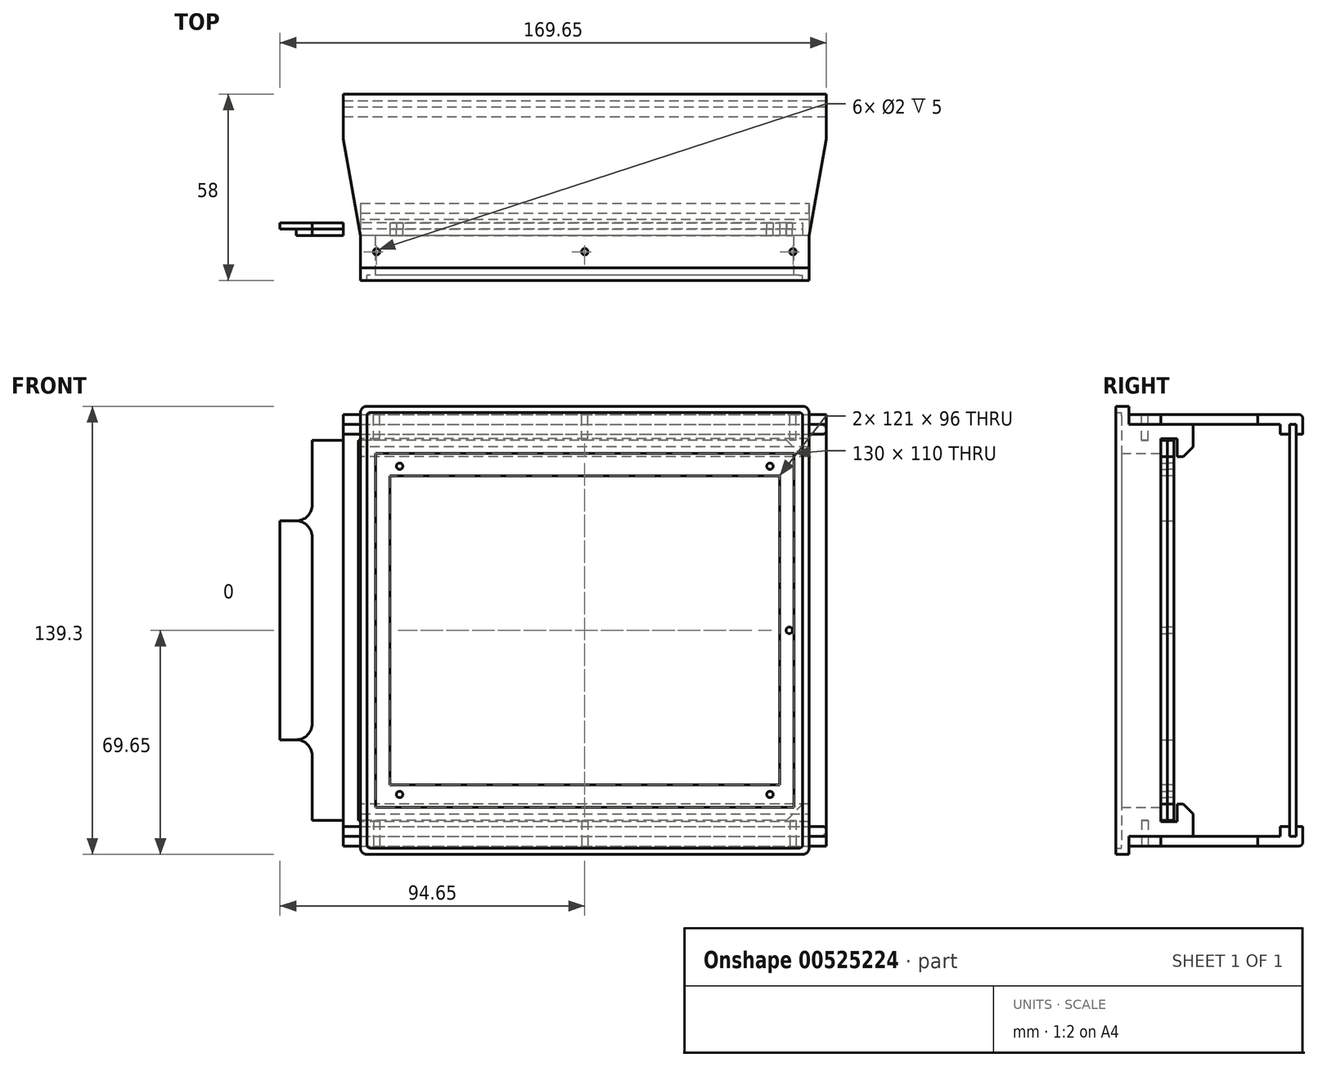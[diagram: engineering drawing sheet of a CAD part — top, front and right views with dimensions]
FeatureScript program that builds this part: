
annotation { "Feature Type Name" : "Feature", "Feature Type Description" : "" }
export const myFeature = defineFeature(function(context is Context, id is Id, definition is map)
    precondition{}
    {
        {
            var Q0;
            Q0=qCreatedBy(makeId("Front.planeOp"),FACE);
            var sketch = newSketch(context, id + "F0", { "sketchPlane" : qUnion([Q0])});
            skLineSegment(sketch, "E0.bottom", {"start": v(69.65, 69.65) * mm, "end": v(-69.65, 69.65) * mm});
            skLineSegment(sketch, "E0.top", {"start": v(69.65, -69.65) * mm, "end": v(-69.65, -69.65) * mm});
            skLineSegment(sketch, "E0.left", {"start": v(69.65, 69.65) * mm, "end": v(69.65, -69.65) * mm});
            skLineSegment(sketch, "E0.right", {"start": v(-69.65, 69.65) * mm, "end": v(-69.65, -69.65) * mm});
            skPoint(sketch, "E0.middle", {"position": v(0, 0) * mm});
            skLineSegment(sketch, "E1.bottom", {"start": v(65, 55) * mm, "end": v(-65, 55) * mm});
            skLineSegment(sketch, "E1.top", {"start": v(65, -55) * mm, "end": v(-65, -55) * mm});
            skLineSegment(sketch, "E1.left", {"start": v(65, 55) * mm, "end": v(65, -55) * mm});
            skLineSegment(sketch, "E1.right", {"start": v(-65, 55) * mm, "end": v(-65, -55) * mm});
            skSolve(sketch);
        }
        {
            var Q0;
            Q0=makeQuery(id+"F0.imprint","IMPRINT",FACE,{"disambiguationData":[TD([[makeQuery(id+"F0.imprint","IMPRINT",EDGE,{"derivedFrom":sQuery(id+"F0.wireOp",EDGE,"E0.bottom")}),1.0]])]});
            extrude(context, id + "F1", {"entities" : qUnion([Q0]), "depth" : 2.3 * mm, "offsetDistance" : 25 * mm});
        }
        {
            var Q0;
            Q0=makeQuery(id+"F1.opExtrude","CAP_FACE",FACE,{"disambiguationData":[OSD([sQuery(id+"F0.wireOp",EDGE,"E0.bottom"),sQuery(id+"F0.wireOp",EDGE,"E0.top"),sQuery(id+"F0.wireOp",EDGE,"E0.left"),sQuery(id+"F0.wireOp",EDGE,"E0.right"),sQuery(id+"F0.wireOp",EDGE,"E1.bottom"),sQuery(id+"F0.wireOp",EDGE,"E1.top"),sQuery(id+"F0.wireOp",EDGE,"E1.left"),sQuery(id+"F0.wireOp",EDGE,"E1.right")])],"isStart":true});
            var sketch = newSketch(context, id + "F2", { "sketchPlane" : qUnion([Q0])});
            skLineSegment(sketch, "E2.0", {"start": v(-65, 55) * mm, "end": v(65, 55) * mm});
            skLineSegment(sketch, "E3.0", {"start": v(-65, 55) * mm, "end": v(-65, -55) * mm});
            skLineSegment(sketch, "E3.1", {"start": v(-65, -55) * mm, "end": v(65, -55) * mm});
            skLineSegment(sketch, "E3.2", {"start": v(65, 55) * mm, "end": v(65, -55) * mm});
            skLineSegment(sketch, "E4.bottom", {"start": v(69.65, 64) * mm, "end": v(-69.65, 64) * mm});
            skLineSegment(sketch, "E4.top", {"start": v(69.65, -64) * mm, "end": v(-69.65, -64) * mm});
            skLineSegment(sketch, "E4.left", {"start": v(69.65, 64) * mm, "end": v(69.65, -64) * mm});
            skLineSegment(sketch, "E4.right", {"start": v(-69.65, 64) * mm, "end": v(-69.65, -64) * mm});
            skPoint(sketch, "E4.middle", {"position": v(0, 0) * mm});
            skSolve(sketch);
        }
        {
            var Q0;
            Q0 = qSketchRegion(id + "F2", true);
            extrude(context, id + "F3", {"entities" : qUnion([Q0]), "operationType" : NewBodyOperationType.ADD, "depth" : 10 * mm, "offsetDistance" : 25 * mm});
        }
        {
            var Q0;
            Q0=makeQuery(id+"F1.opExtrude","CAP_FACE",FACE,{"disambiguationData":[OSD([sQuery(id+"F0.wireOp",EDGE,"E0.bottom"),sQuery(id+"F0.wireOp",EDGE,"E0.top"),sQuery(id+"F0.wireOp",EDGE,"E0.left"),sQuery(id+"F0.wireOp",EDGE,"E0.right"),sQuery(id+"F0.wireOp",EDGE,"E1.bottom"),sQuery(id+"F0.wireOp",EDGE,"E1.top"),sQuery(id+"F0.wireOp",EDGE,"E1.left"),sQuery(id+"F0.wireOp",EDGE,"E1.right")])],"isStart":false});
            var sketch = newSketch(context, id + "F4", { "sketchPlane" : qUnion([Q0])});
            skLineSegment(sketch, "E5.0", {"start": v(69.65, 69.65) * mm, "end": v(-69.65, 69.65) * mm});
            skLineSegment(sketch, "E5.1", {"start": v(-69.65, 69.65) * mm, "end": v(-69.65, -69.65) * mm});
            skLineSegment(sketch, "E5.2", {"start": v(69.65, -69.65) * mm, "end": v(-69.65, -69.65) * mm});
            skLineSegment(sketch, "E5.3", {"start": v(69.65, 69.65) * mm, "end": v(69.65, -69.65) * mm});
            skLineSegment(sketch, "E6.0", {"start": v(67.65, 67.65) * mm, "end": v(-67.65, 67.65) * mm});
            skLineSegment(sketch, "E6.1", {"start": v(67.65, 67.65) * mm, "end": v(67.65, -67.65) * mm});
            skLineSegment(sketch, "E6.2", {"start": v(67.65, -67.65) * mm, "end": v(-67.65, -67.65) * mm});
            skLineSegment(sketch, "E6.3", {"start": v(-67.65, 67.65) * mm, "end": v(-67.65, -67.65) * mm});
            skSolve(sketch);
        }
        {
            var Q0;
            Q0 = qSketchRegion(id + "F4", true);
            extrude(context, id + "F5", {"entities" : qUnion([Q0]), "operationType" : NewBodyOperationType.ADD, "depth" : 1.7 * mm, "offsetDistance" : 25 * mm});
        }
        {
            var Q0;
            Q0=makeQuery(id+"F5.opExtrude","SWEPT_EDGE",EDGE,{"disambiguationData":[OSD([sQuery(id+"F4.wireOp",EDGE,"E6.0"),sQuery(id+"F4.wireOp",EDGE,"E6.3")])]});
            var Q1;
            Q1=makeQuery(id+"F5.opExtrude","SWEPT_EDGE",EDGE,{"disambiguationData":[OSD([sQuery(id+"F4.wireOp",EDGE,"E6.0"),sQuery(id+"F4.wireOp",EDGE,"E6.1")])]});
            var Q2;
            Q2=makeQuery(id+"F5.opExtrude","SWEPT_EDGE",EDGE,{"disambiguationData":[OSD([sQuery(id+"F4.wireOp",EDGE,"E6.2"),sQuery(id+"F4.wireOp",EDGE,"E6.3")])]});
            var Q3;
            Q3=makeQuery(id+"F5.opExtrude","SWEPT_EDGE",EDGE,{"disambiguationData":[OSD([sQuery(id+"F4.wireOp",EDGE,"E6.1"),sQuery(id+"F4.wireOp",EDGE,"E6.2")])]});
            fillet(context, id + "F6", {"entities" : qUnion([Q0, Q1, Q2, Q3]), "radius" : 1 * mm, "tangentPropagation" : true, "allowEdgeOverflow" : false});
        }
        {
            var Q0;
            Q0=makeQuery(id+"F5.boolean.opBoolean","MERGE",EDGE,{"derivedFrom":[makeQuery(id+"F1.opExtrude","SWEPT_EDGE",EDGE,{"disambiguationData":[OSD([sQuery(id+"F0.wireOp",EDGE,"E0.top"),sQuery(id+"F0.wireOp",EDGE,"E0.right")])]}),makeQuery(id+"F5.opExtrude","SWEPT_EDGE",EDGE,{"disambiguationData":[OSD([sQuery(id+"F4.wireOp",EDGE,"E5.1"),sQuery(id+"F4.wireOp",EDGE,"E5.2")])]})]});
            var Q1;
            Q1=makeQuery(id+"F5.boolean.opBoolean","MERGE",EDGE,{"derivedFrom":[makeQuery(id+"F1.opExtrude","SWEPT_EDGE",EDGE,{"disambiguationData":[OSD([sQuery(id+"F0.wireOp",EDGE,"E0.top"),sQuery(id+"F0.wireOp",EDGE,"E0.left")])]}),makeQuery(id+"F5.opExtrude","SWEPT_EDGE",EDGE,{"disambiguationData":[OSD([sQuery(id+"F4.wireOp",EDGE,"E5.2"),sQuery(id+"F4.wireOp",EDGE,"E5.3")])]})]});
            var Q2;
            Q2=makeQuery(id+"F5.boolean.opBoolean","MERGE",EDGE,{"derivedFrom":[makeQuery(id+"F1.opExtrude","SWEPT_EDGE",EDGE,{"disambiguationData":[OSD([sQuery(id+"F0.wireOp",EDGE,"E0.bottom"),sQuery(id+"F0.wireOp",EDGE,"E0.left")])]}),makeQuery(id+"F5.opExtrude","SWEPT_EDGE",EDGE,{"disambiguationData":[OSD([sQuery(id+"F4.wireOp",EDGE,"E5.0"),sQuery(id+"F4.wireOp",EDGE,"E5.3")])]})]});
            var Q3;
            Q3=makeQuery(id+"F5.boolean.opBoolean","MERGE",EDGE,{"derivedFrom":[makeQuery(id+"F1.opExtrude","SWEPT_EDGE",EDGE,{"disambiguationData":[OSD([sQuery(id+"F0.wireOp",EDGE,"E0.bottom"),sQuery(id+"F0.wireOp",EDGE,"E0.right")])]}),makeQuery(id+"F5.opExtrude","SWEPT_EDGE",EDGE,{"disambiguationData":[OSD([sQuery(id+"F4.wireOp",EDGE,"E5.0"),sQuery(id+"F4.wireOp",EDGE,"E5.1")])]})]});
            fillet(context, id + "F7", {"entities" : qUnion([Q0, Q1, Q2, Q3]), "radius" : 2 * mm, "tangentPropagation" : true, "allowEdgeOverflow" : false});
        }
        {
            var Q0;
            Q0=makeQuery(id+"F3.opExtrude","CAP_FACE",FACE,{"disambiguationData":[OSD([sQuery(id+"F2.wireOp",EDGE,"E2.0"),sQuery(id+"F2.wireOp",EDGE,"E3.0"),sQuery(id+"F2.wireOp",EDGE,"E3.1"),sQuery(id+"F2.wireOp",EDGE,"E3.2"),sQuery(id+"F2.wireOp",EDGE,"E4.bottom"),sQuery(id+"F2.wireOp",EDGE,"E4.top"),sQuery(id+"F2.wireOp",EDGE,"E4.left"),sQuery(id+"F2.wireOp",EDGE,"E4.right")])],"isStart":false});
            var sketch = newSketch(context, id + "F8", { "sketchPlane" : qUnion([Q0])});
            skLineSegment(sketch, "E7.bottom", {"start": v(60.5, 48) * mm, "end": v(-60.5, 48) * mm});
            skLineSegment(sketch, "E7.top", {"start": v(60.5, -48) * mm, "end": v(-60.5, -48) * mm});
            skLineSegment(sketch, "E7.left", {"start": v(60.5, 48) * mm, "end": v(60.5, -48) * mm});
            skLineSegment(sketch, "E7.right", {"start": v(-60.5, 48) * mm, "end": v(-60.5, -48) * mm});
            skPoint(sketch, "E7.middle", {"position": v(0, 0) * mm});
            skLineSegment(sketch, "E8.bottom", {"start": v(-67.65, 59) * mm, "end": v(94.65, 59) * mm});
            skLineSegment(sketch, "E8.top", {"start": v(-67.65, -59) * mm, "end": v(94.65, -59) * mm});
            skLineSegment(sketch, "E8.left", {"start": v(-67.65, 59) * mm, "end": v(-67.65, -59) * mm});
            skLineSegment(sketch, "E8.right", {"start": v(94.65, 59) * mm, "end": v(94.65, -59) * mm});
            skLineSegment(sketch, "E9", {"start": v(-80.22, 0) * mm, "end": v(93.95, 0) * mm, "construction": true});
            skPoint(sketch, "E9.endSnap0", {"position": v(-69.65, 0) * mm});
            skSolve(sketch);
        }
        {
            var Q0;
            Q0 = qSketchRegion(id + "F8", true);
            extrude(context, id + "F9", {"entities" : qUnion([Q0]), "depth" : 2 * mm, "offsetDistance" : 25 * mm});
        }
        {
            var Q0;
            Q0=makeQuery(id+"F9.opExtrude","CAP_FACE",FACE,{"disambiguationData":[OSD([sQuery(id+"F8.wireOp",EDGE,"E7.bottom"),sQuery(id+"F8.wireOp",EDGE,"E7.top"),sQuery(id+"F8.wireOp",EDGE,"E7.left"),sQuery(id+"F8.wireOp",EDGE,"E7.right"),sQuery(id+"F8.wireOp",EDGE,"E8.bottom"),sQuery(id+"F8.wireOp",EDGE,"E8.top"),sQuery(id+"F8.wireOp",EDGE,"E8.left"),sQuery(id+"F8.wireOp",EDGE,"E8.right")])],"isStart":false});
            var sketch = newSketch(context, id + "F10", { "sketchPlane" : qUnion([Q0])});
            skLineSegment(sketch, "E10.bottom", {"start": v(62.5, 50) * mm, "end": v(-62.5, 50) * mm, "construction": true});
            skLineSegment(sketch, "E10.top", {"start": v(62.5, -50) * mm, "end": v(-62.5, -50) * mm, "construction": true});
            skLineSegment(sketch, "E10.left", {"start": v(62.5, 50) * mm, "end": v(62.5, -50) * mm, "construction": true});
            skLineSegment(sketch, "E10.right", {"start": v(-62.5, 50) * mm, "end": v(-62.5, -50) * mm, "construction": true});
            skPoint(sketch, "E10.middle", {"position": v(0, 0) * mm});
            skCircle(sketch, "E11", {"center": v(-57.5, 51) * mm, "radius": 1 * mm});
            skCircle(sketch, "E12", {"center": v(57.5, 51) * mm, "radius": 1 * mm});
            skCircle(sketch, "E13", {"center": v(57.5, -51) * mm, "radius": 1 * mm});
            skCircle(sketch, "E14", {"center": v(-57.5, -51) * mm, "radius": 1 * mm});
            skLineSegment(sketch, "E15", {"start": v(-12.77, 0) * mm, "end": v(-78.05, 0) * mm, "construction": true});
            skPoint(sketch, "E15.startSnap0", {"position": v(-67.65, 0) * mm});
            skPoint(sketch, "E15.endSnap0", {"position": v(-67.65, 0) * mm});
            skCircle(sketch, "E16", {"center": v(-63.5, 0) * mm, "radius": 1 * mm});
            skSolve(sketch);
        }
        {
            var Q0;
            Q0 = qSketchRegion(id + "F10", true);
            extrude(context, id + "F11", {"entities" : qUnion([Q0]), "operationType" : NewBodyOperationType.REMOVE, "oppositeDirection" : true, "depth" : 25 * mm, "offsetDistance" : 25 * mm});
        }
        {
            var Q0;
            Q0=makeQuery(id+"F9.opExtrude","SWEPT_EDGE",EDGE,{"disambiguationData":[OSD([sQuery(id+"F8.wireOp",EDGE,"E8.top"),sQuery(id+"F8.wireOp",EDGE,"E8.left")])]});
            var Q1;
            Q1=makeQuery(id+"F9.opExtrude","SWEPT_EDGE",EDGE,{"disambiguationData":[OSD([sQuery(id+"F8.wireOp",EDGE,"E8.bottom"),sQuery(id+"F8.wireOp",EDGE,"E8.left")])]});
            chamfer(context, id + "F12", {"entities" : qUnion([Q0, Q1]), "width" : 5 * mm, "tangentPropagation" : true});
        }
        {
            var Q0;
            Q0=makeQuery(id+"F9.opExtrude","CAP_FACE",FACE,{"disambiguationData":[OSD([sQuery(id+"F8.wireOp",EDGE,"E7.bottom"),sQuery(id+"F8.wireOp",EDGE,"E7.top"),sQuery(id+"F8.wireOp",EDGE,"E7.left"),sQuery(id+"F8.wireOp",EDGE,"E7.right"),sQuery(id+"F8.wireOp",EDGE,"E8.bottom"),sQuery(id+"F8.wireOp",EDGE,"E8.top"),sQuery(id+"F8.wireOp",EDGE,"E8.left"),sQuery(id+"F8.wireOp",EDGE,"E8.right")])],"isStart":false});
            var sketch = newSketch(context, id + "F13", { "sketchPlane" : qUnion([Q0])});
            skSolve(sketch);
        }
        {
            var Q0;
            {var subQ1=sQuery(id+"F8.wireOp",EDGE,"E7.bottom");Q0=makeQuery(id+"F13.imprint","IMPRINT",FACE,{"disambiguationData":[TD([[makeQuery(id+"F13.imprint","IMPRINT",EDGE,{"derivedFrom":makeQuery(id+"F9.opExtrude","CAP_EDGE",EDGE,{"disambiguationData":[OSD([subQ1])],"isStart":false})}),-1.0]])]});}
            extrude(context, id + "F14", {"entities" : qUnion([Q0]), "depth" : 2 * mm, "offsetDistance" : 25 * mm});
        }
        {
            var Q0;
            Q0=makeQuery(id+"F14.opExtrude","CAP_FACE",FACE,{"disambiguationData":[OSD([sQuery(id+"F8.wireOp",EDGE,"E7.bottom"),sQuery(id+"F8.wireOp",EDGE,"E7.top"),sQuery(id+"F8.wireOp",EDGE,"E7.left"),sQuery(id+"F8.wireOp",EDGE,"E7.right"),sQuery(id+"F8.wireOp",EDGE,"E8.bottom"),sQuery(id+"F8.wireOp",EDGE,"E8.top"),sQuery(id+"F8.wireOp",EDGE,"E8.left"),sQuery(id+"F8.wireOp",EDGE,"E8.right"),sQuery(id+"F10.wireOp",EDGE,"E11"),sQuery(id+"F10.wireOp",EDGE,"E12"),sQuery(id+"F10.wireOp",EDGE,"E13"),sQuery(id+"F10.wireOp",EDGE,"E14"),sQuery(id+"F10.wireOp",EDGE,"E16")])],"isStart":false});
            var sketch = newSketch(context, id + "F15", { "sketchPlane" : qUnion([Q0])});
            skLineSegment(sketch, "E17", {"start": v(0, 0) * mm, "end": v(113.47, 0) * mm, "construction": true});
            skPoint(sketch, "E17.endSnap0", {"position": v(94.65, 0) * mm});
            skLineSegment(sketch, "E18", {"start": v(84.65, 59) * mm, "end": v(84.65, 34) * mm});
            skLineSegment(sketch, "E19", {"start": v(84.65, 34) * mm, "end": v(94.65, 34) * mm});
            skLineSegment(sketch, "E20", {"start": v(94.65, 34) * mm, "end": v(94.65, 59) * mm});
            skLineSegment(sketch, "E21", {"start": v(94.65, 59) * mm, "end": v(84.65, 59) * mm});
            skLineSegment(sketch, "E22.bottom", {"start": v(94.65, -59) * mm, "end": v(84.65, -59) * mm});
            skLineSegment(sketch, "E22.top", {"start": v(94.65, -34) * mm, "end": v(84.65, -34) * mm});
            skLineSegment(sketch, "E22.left", {"start": v(94.65, -59) * mm, "end": v(94.65, -34) * mm});
            skLineSegment(sketch, "E22.right", {"start": v(84.65, -59) * mm, "end": v(84.65, -34) * mm});
            skSolve(sketch);
        }
        {
            var Q0;
            Q0 = qSketchRegion(id + "F15", true);
            extrude(context, id + "F16", {"entities" : qUnion([Q0]), "operationType" : NewBodyOperationType.REMOVE, "oppositeDirection" : true, "depth" : 25 * mm, "offsetDistance" : 25 * mm});
        }
        {
            var Q0;
            Q0=makeQuery(id+"F16.boolean.opBoolean","COPY",EDGE,{"derivedFrom":makeQuery(id+"F16.opExtrude","SWEPT_EDGE",EDGE,{"disambiguationData":[OSD([sQuery(id+"F8.wireOp",EDGE,"E8.top"),sQuery(id+"F15.wireOp",EDGE,"E22.bottom"),sQuery(id+"F15.wireOp",EDGE,"E22.right")])]})});
            var Q1;
            Q1=makeQuery(id+"F16.boolean.opBoolean","COPY",EDGE,{"derivedFrom":makeQuery(id+"F16.opExtrude","SWEPT_EDGE",EDGE,{"disambiguationData":[OSD([sQuery(id+"F15.wireOp",EDGE,"E22.top"),sQuery(id+"F15.wireOp",EDGE,"E22.right")])]})});
            var Q2;
            Q2=makeQuery(id+"F16.boolean.opBoolean","COPY",EDGE,{"derivedFrom":makeQuery(id+"F16.opExtrude","SWEPT_EDGE",EDGE,{"disambiguationData":[OSD([sQuery(id+"F8.wireOp",EDGE,"E8.right"),sQuery(id+"F15.wireOp",EDGE,"E22.top"),sQuery(id+"F15.wireOp",EDGE,"E22.left")])]})});
            var Q3;
            Q3=makeQuery(id+"F16.boolean.opBoolean","COPY",EDGE,{"derivedFrom":makeQuery(id+"F16.opExtrude","SWEPT_EDGE",EDGE,{"disambiguationData":[OSD([sQuery(id+"F8.wireOp",EDGE,"E8.right"),sQuery(id+"F15.wireOp",EDGE,"E19"),sQuery(id+"F15.wireOp",EDGE,"E20")])]})});
            var Q4;
            Q4=makeQuery(id+"F16.boolean.opBoolean","COPY",EDGE,{"derivedFrom":makeQuery(id+"F16.opExtrude","SWEPT_EDGE",EDGE,{"disambiguationData":[OSD([sQuery(id+"F15.wireOp",EDGE,"E18"),sQuery(id+"F15.wireOp",EDGE,"E19")])]})});
            var Q5;
            Q5=makeQuery(id+"F16.boolean.opBoolean","COPY",EDGE,{"derivedFrom":makeQuery(id+"F16.opExtrude","SWEPT_EDGE",EDGE,{"disambiguationData":[OSD([sQuery(id+"F8.wireOp",EDGE,"E8.bottom"),sQuery(id+"F15.wireOp",EDGE,"E18"),sQuery(id+"F15.wireOp",EDGE,"E21")])]})});
            fillet(context, id + "F17", {"entities" : qUnion([Q0, Q1, Q2, Q3, Q4, Q5]), "radius" : 5 * mm, "tangentPropagation" : true, "allowEdgeOverflow" : false});
        }
        {
            var Q0;
            Q0=makeQuery(id+"F9.opExtrude","CAP_FACE",FACE,{"disambiguationData":[OSD([sQuery(id+"F8.wireOp",EDGE,"E7.bottom"),sQuery(id+"F8.wireOp",EDGE,"E7.top"),sQuery(id+"F8.wireOp",EDGE,"E7.left"),sQuery(id+"F8.wireOp",EDGE,"E7.right"),sQuery(id+"F8.wireOp",EDGE,"E8.bottom"),sQuery(id+"F8.wireOp",EDGE,"E8.top"),sQuery(id+"F8.wireOp",EDGE,"E8.left"),sQuery(id+"F8.wireOp",EDGE,"E8.right")])],"isStart":false});
            var sketch = newSketch(context, id + "F18", { "sketchPlane" : qUnion([Q0])});
            skLineSegment(sketch, "E23", {"start": v(0, 0) * mm, "end": v(104.62, 0) * mm, "construction": true});
            skPoint(sketch, "E23.endSnap0", {"position": v(60.5, 0) * mm});
            skLineSegment(sketch, "E24.bottom", {"start": v(94.65, 34) * mm, "end": v(84.65, 34) * mm});
            skLineSegment(sketch, "E24.top", {"start": v(94.65, -34) * mm, "end": v(84.65, -34) * mm});
            skLineSegment(sketch, "E24.left", {"start": v(94.65, 34) * mm, "end": v(94.65, -34) * mm});
            skLineSegment(sketch, "E24.right", {"start": v(84.65, 34) * mm, "end": v(84.65, -34) * mm});
            skSolve(sketch);
        }
        {
            var Q0;
            Q0 = qSketchRegion(id + "F18", true);
            extrude(context, id + "F19", {"entities" : qUnion([Q0]), "operationType" : NewBodyOperationType.REMOVE, "oppositeDirection" : true, "depth" : 25 * mm, "offsetDistance" : 25 * mm});
        }
        {
            var Q0;
            Q0=makeQuery(id+"F9.opExtrude","SWEPT_EDGE",EDGE,{"disambiguationData":[OSD([sQuery(id+"F8.wireOp",EDGE,"E8.top"),sQuery(id+"F8.wireOp",EDGE,"E8.right")])]});
            var Q1;
            Q1=makeQuery(id+"F19.boolean.opBoolean","COPY",EDGE,{"derivedFrom":makeQuery(id+"F19.opExtrude","SWEPT_EDGE",EDGE,{"disambiguationData":[OSD([sQuery(id+"F8.wireOp",EDGE,"E8.right"),sQuery(id+"F18.wireOp",EDGE,"E24.top"),sQuery(id+"F18.wireOp",EDGE,"E24.left")])]})});
            var Q2;
            Q2=makeQuery(id+"F19.boolean.opBoolean","COPY",EDGE,{"derivedFrom":makeQuery(id+"F19.opExtrude","SWEPT_EDGE",EDGE,{"disambiguationData":[OSD([sQuery(id+"F18.wireOp",EDGE,"E24.top"),sQuery(id+"F18.wireOp",EDGE,"E24.right")])]})});
            var Q3;
            Q3=makeQuery(id+"F19.boolean.opBoolean","COPY",EDGE,{"derivedFrom":makeQuery(id+"F19.opExtrude","SWEPT_EDGE",EDGE,{"disambiguationData":[OSD([sQuery(id+"F18.wireOp",EDGE,"E24.bottom"),sQuery(id+"F18.wireOp",EDGE,"E24.right")])]})});
            var Q4;
            Q4=makeQuery(id+"F19.boolean.opBoolean","COPY",EDGE,{"derivedFrom":makeQuery(id+"F19.opExtrude","SWEPT_EDGE",EDGE,{"disambiguationData":[OSD([sQuery(id+"F8.wireOp",EDGE,"E8.right"),sQuery(id+"F18.wireOp",EDGE,"E24.bottom"),sQuery(id+"F18.wireOp",EDGE,"E24.left")])]})});
            var Q5;
            Q5=makeQuery(id+"F9.opExtrude","SWEPT_EDGE",EDGE,{"disambiguationData":[OSD([sQuery(id+"F8.wireOp",EDGE,"E8.bottom"),sQuery(id+"F8.wireOp",EDGE,"E8.right")])]});
            fillet(context, id + "F20", {"entities" : qUnion([Q0, Q1, Q2, Q3, Q4, Q5]), "radius" : 5 * mm, "tangentPropagation" : true, "allowEdgeOverflow" : false});
        }
        {
            var Q0;
            Q0=makeQuery(id+"F3.opExtrude","CAP_FACE",FACE,{"disambiguationData":[OSD([sQuery(id+"F2.wireOp",EDGE,"E2.0"),sQuery(id+"F2.wireOp",EDGE,"E3.0"),sQuery(id+"F2.wireOp",EDGE,"E3.1"),sQuery(id+"F2.wireOp",EDGE,"E3.2"),sQuery(id+"F2.wireOp",EDGE,"E4.bottom"),sQuery(id+"F2.wireOp",EDGE,"E4.top"),sQuery(id+"F2.wireOp",EDGE,"E4.left"),sQuery(id+"F2.wireOp",EDGE,"E4.right")])],"isStart":false});
            var sketch = newSketch(context, id + "F21", { "sketchPlane" : qUnion([Q0])});
            skLineSegment(sketch, "E25.bottom", {"start": v(-69.65, 64) * mm, "end": v(69.65, 64) * mm});
            skLineSegment(sketch, "E25.top", {"start": v(-69.65, 59.5) * mm, "end": v(69.65, 59.5) * mm});
            skLineSegment(sketch, "E25.left", {"start": v(-69.65, 64) * mm, "end": v(-69.65, 59.5) * mm});
            skLineSegment(sketch, "E25.right", {"start": v(69.65, 64) * mm, "end": v(69.65, 59.5) * mm});
            skLineSegment(sketch, "E26.bottom", {"start": v(-69.65, -64) * mm, "end": v(69.65, -64) * mm});
            skLineSegment(sketch, "E26.top", {"start": v(-69.65, -59.5) * mm, "end": v(69.65, -59.5) * mm});
            skLineSegment(sketch, "E26.left", {"start": v(-69.65, -64) * mm, "end": v(-69.65, -59.5) * mm});
            skLineSegment(sketch, "E26.right", {"start": v(69.65, -64) * mm, "end": v(69.65, -59.5) * mm});
            skSolve(sketch);
        }
        {
            var Q0;
            Q0 = qSketchRegion(id + "F21", true);
            extrude(context, id + "F22", {"entities" : qUnion([Q0]), "operationType" : NewBodyOperationType.ADD, "depth" : 5 * mm, "offsetDistance" : 25 * mm});
        }
        {
            var Q0;
            Q0=makeQuery(id+"F22.opExtrude","CAP_FACE",FACE,{"disambiguationData":[OSD([sQuery(id+"F21.wireOp",EDGE,"E25.bottom"),sQuery(id+"F21.wireOp",EDGE,"E25.top"),sQuery(id+"F21.wireOp",EDGE,"E25.left"),sQuery(id+"F21.wireOp",EDGE,"E25.right")])],"isStart":false});
            var sketch = newSketch(context, id + "F23", { "sketchPlane" : qUnion([Q0])});
            skLineSegment(sketch, "E27.bottom", {"start": v(-69.65, 64) * mm, "end": v(69.65, 64) * mm});
            skLineSegment(sketch, "E27.top", {"start": v(-69.65, 54) * mm, "end": v(69.65, 54) * mm});
            skLineSegment(sketch, "E27.left", {"start": v(-69.65, 64) * mm, "end": v(-69.65, 54) * mm});
            skLineSegment(sketch, "E27.right", {"start": v(69.65, 64) * mm, "end": v(69.65, 54) * mm});
            skLineSegment(sketch, "E28.bottom", {"start": v(-69.65, -64) * mm, "end": v(69.65, -64) * mm});
            skLineSegment(sketch, "E28.top", {"start": v(-69.65, -54) * mm, "end": v(69.65, -54) * mm});
            skLineSegment(sketch, "E28.left", {"start": v(-69.65, -64) * mm, "end": v(-69.65, -54) * mm});
            skLineSegment(sketch, "E28.right", {"start": v(69.65, -64) * mm, "end": v(69.65, -54) * mm});
            skSolve(sketch);
        }
        {
            var Q0;
            Q0 = qSketchRegion(id + "F23", true);
            extrude(context, id + "F24", {"entities" : qUnion([Q0]), "operationType" : NewBodyOperationType.ADD, "depth" : 5 * mm, "offsetDistance" : 25 * mm});
        }
        {
            var Q0;
            Q0=makeQuery(id+"F24.opExtrude","CAP_EDGE",EDGE,{"disambiguationData":[OSD([sQuery(id+"F23.wireOp",EDGE,"E27.top")])],"isStart":false});
            var Q1;
            Q1=makeQuery(id+"F24.opExtrude","CAP_EDGE",EDGE,{"disambiguationData":[OSD([sQuery(id+"F23.wireOp",EDGE,"E28.top")])],"isStart":false});
            chamfer(context, id + "F25", {"entities" : qUnion([Q0, Q1]), "width" : 3 * mm, "tangentPropagation" : true});
        }
        {
            var Q0;
            Q0=qCreatedBy(makeId("Right.planeOp"),FACE);
            var sketch = newSketch(context, id + "F26", { "sketchPlane" : qUnion([Q0])});
            skLineSegment(sketch, "E29", {"start": v(0, 64) * mm, "end": v(47, 64) * mm});
            skLineSegment(sketch, "E30", {"start": v(47, 64) * mm, "end": v(47, 61) * mm});
            skLineSegment(sketch, "E31", {"start": v(47, 61) * mm, "end": v(50, 61) * mm});
            skLineSegment(sketch, "E32", {"start": v(50, 61) * mm, "end": v(50, 64) * mm});
            skLineSegment(sketch, "E33", {"start": v(50, 64) * mm, "end": v(52, 64) * mm});
            skLineSegment(sketch, "E34", {"start": v(52, 64) * mm, "end": v(52, 61) * mm});
            skLineSegment(sketch, "E35", {"start": v(52, 61) * mm, "end": v(54, 61) * mm});
            skLineSegment(sketch, "E36", {"start": v(54, 61) * mm, "end": v(54, 67) * mm});
            skLineSegment(sketch, "E37", {"start": v(54, 67) * mm, "end": v(0, 67) * mm});
            skLineSegment(sketch, "E38", {"start": v(0, 67) * mm, "end": v(0, 64) * mm});
            skLineSegment(sketch, "E39", {"start": v(0, 0) * mm, "end": v(91.53, 0) * mm, "construction": true});
            skLineSegment(sketch, "E40.MirrorCS", {"start": v(0, -67) * mm, "end": v(0, -64) * mm});
            skLineSegment(sketch, "E41.MirrorCS", {"start": v(52, -64) * mm, "end": v(52, -61) * mm});
            skLineSegment(sketch, "E42.MirrorCS", {"start": v(52, -61) * mm, "end": v(54, -61) * mm});
            skLineSegment(sketch, "E43.MirrorCS", {"start": v(50, -64) * mm, "end": v(52, -64) * mm});
            skLineSegment(sketch, "E44.MirrorCS", {"start": v(50, -61) * mm, "end": v(50, -64) * mm});
            skLineSegment(sketch, "E45.MirrorCS", {"start": v(47, -61) * mm, "end": v(50, -61) * mm});
            skLineSegment(sketch, "E46.MirrorCS", {"start": v(47, -64) * mm, "end": v(47, -61) * mm});
            skLineSegment(sketch, "E47.MirrorCS", {"start": v(54, -67) * mm, "end": v(0, -67) * mm});
            skLineSegment(sketch, "E48.MirrorCS", {"start": v(54, -61) * mm, "end": v(54, -67) * mm});
            skLineSegment(sketch, "E49.MirrorCS", {"start": v(0, -64) * mm, "end": v(47, -64) * mm});
            skSolve(sketch);
        }
        {
            var Q0;
            Q0 = qSketchRegion(id + "F26", true);
            var Q1;
            Q1=makeQuery(id+"F24.boolean.opBoolean","MERGE",FACE,{"derivedFrom":[makeQuery(id+"F22.boolean.opBoolean","MERGE",FACE,{"derivedFrom":[makeQuery(id+"F5.boolean.opBoolean","MERGE",FACE,{"derivedFrom":[makeQuery(id+"F3.boolean.opBoolean","MERGE",FACE,{"derivedFrom":[makeQuery(id+"F1.opExtrude","SWEPT_FACE",FACE,{"disambiguationData":[OSD([sQuery(id+"F0.wireOp",EDGE,"E0.right")])]}),makeQuery(id+"F3.opExtrude","SWEPT_FACE",FACE,{"disambiguationData":[OSD([sQuery(id+"F2.wireOp",EDGE,"E4.left")])]})]}),makeQuery(id+"F5.opExtrude","SWEPT_FACE",FACE,{"disambiguationData":[OSD([sQuery(id+"F4.wireOp",EDGE,"E5.1")])]})]}),makeQuery(id+"F22.opExtrude","SWEPT_FACE",FACE,{"disambiguationData":[OSD([sQuery(id+"F21.wireOp",EDGE,"E25.right")])]}),makeQuery(id+"F22.opExtrude","SWEPT_FACE",FACE,{"disambiguationData":[OSD([sQuery(id+"F21.wireOp",EDGE,"E26.right")])]})]}),makeQuery(id+"F24.opExtrude","SWEPT_FACE",FACE,{"disambiguationData":[OSD([sQuery(id+"F23.wireOp",EDGE,"E27.right")])]}),makeQuery(id+"F24.opExtrude","SWEPT_FACE",FACE,{"disambiguationData":[OSD([sQuery(id+"F23.wireOp",EDGE,"E28.right")])]})]});
            extrude(context, id + "F27", {"entities" : qUnion([Q0]), "endBound" : BoundingType.SYMMETRIC, "oppositeDirection" : true, "depth" : 150 * mm, "endBoundEntityFace" : qUnion([Q1]), "offsetDistance" : 25 * mm});
        }
        {
            var Q0;
            Q0=makeQuery(id+"F27.opExtrude","CAP_FACE",FACE,{"disambiguationData":[OSD([sQuery(id+"F26.wireOp",EDGE,"E29"),sQuery(id+"F26.wireOp",EDGE,"E30"),sQuery(id+"F26.wireOp",EDGE,"E31"),sQuery(id+"F26.wireOp",EDGE,"E32"),sQuery(id+"F26.wireOp",EDGE,"E33"),sQuery(id+"F26.wireOp",EDGE,"E34"),sQuery(id+"F26.wireOp",EDGE,"E35"),sQuery(id+"F26.wireOp",EDGE,"E36"),sQuery(id+"F26.wireOp",EDGE,"E37"),sQuery(id+"F26.wireOp",EDGE,"E38")])],"isStart":true});
            var sketch = newSketch(context, id + "F28", { "sketchPlane" : qUnion([Q0])});
            skLineSegment(sketch, "E50.bottom", {"start": v(50, 64) * mm, "end": v(52, 64) * mm});
            skLineSegment(sketch, "E50.top", {"start": v(50, -64) * mm, "end": v(52, -64) * mm});
            skLineSegment(sketch, "E50.left", {"start": v(50, 64) * mm, "end": v(50, -64) * mm});
            skLineSegment(sketch, "E50.right", {"start": v(52, 64) * mm, "end": v(52, -64) * mm});
            skSolve(sketch);
        }
        {
            var Q0;
            Q0 = qSketchRegion(id + "F28", true);
            var Q1;
            Q1=makeQuery(id+"F27.opExtrude","CAP_FACE",FACE,{"disambiguationData":[OSD([sQuery(id+"F26.wireOp",EDGE,"E29"),sQuery(id+"F26.wireOp",EDGE,"E30"),sQuery(id+"F26.wireOp",EDGE,"E31"),sQuery(id+"F26.wireOp",EDGE,"E32"),sQuery(id+"F26.wireOp",EDGE,"E33"),sQuery(id+"F26.wireOp",EDGE,"E34"),sQuery(id+"F26.wireOp",EDGE,"E35"),sQuery(id+"F26.wireOp",EDGE,"E36"),sQuery(id+"F26.wireOp",EDGE,"E37"),sQuery(id+"F26.wireOp",EDGE,"E38")])],"isStart":false});
            extrude(context, id + "F29", {"entities" : qUnion([Q0]), "endBound" : BoundingType.UP_TO_SURFACE, "oppositeDirection" : true, "depth" : 25 * mm, "endBoundEntityFace" : qUnion([Q1]), "offsetDistance" : 25 * mm});
        }
        {
            var Q0;
            Q0=makeQuery(id+"F29.opExtrude","CAP_EDGE",EDGE,{"disambiguationData":[OSD([sQuery(id+"F28.wireOp",EDGE,"E50.bottom")])],"isStart":true});
            var Q1;
            Q1=makeQuery(id+"F29.opExtrude","TWEAK_EDGE",EDGE,{"derivedFrom":[makeQuery(id+"F27.opExtrude","CAP_FACE",FACE,{"disambiguationData":[OSD([sQuery(id+"F0.wireOp",EDGE,"E0.right"),sQuery(id+"F2.wireOp",EDGE,"E4.left"),sQuery(id+"F4.wireOp",EDGE,"E5.1"),sQuery(id+"F21.wireOp",EDGE,"E25.right"),sQuery(id+"F21.wireOp",EDGE,"E26.right"),sQuery(id+"F23.wireOp",EDGE,"E27.right"),sQuery(id+"F23.wireOp",EDGE,"E28.right")]),OD(0.0)],"isStart":false}),makeQuery(id+"F28.imprint","IMPRINT",EDGE,{"derivedFrom":sQuery(id+"F28.wireOp",EDGE,"E50.bottom")})]});
            var Q2;
            Q2=makeQuery(id+"F29.opExtrude","TWEAK_EDGE",EDGE,{"derivedFrom":[makeQuery(id+"F27.opExtrude","CAP_FACE",FACE,{"disambiguationData":[OSD([sQuery(id+"F0.wireOp",EDGE,"E0.right"),sQuery(id+"F2.wireOp",EDGE,"E4.left"),sQuery(id+"F4.wireOp",EDGE,"E5.1"),sQuery(id+"F21.wireOp",EDGE,"E25.right"),sQuery(id+"F21.wireOp",EDGE,"E26.right"),sQuery(id+"F23.wireOp",EDGE,"E27.right"),sQuery(id+"F23.wireOp",EDGE,"E28.right")]),OD(0.0)],"isStart":false}),makeQuery(id+"F28.imprint","IMPRINT",EDGE,{"derivedFrom":sQuery(id+"F28.wireOp",EDGE,"E50.top")})]});
            var Q3;
            Q3=makeQuery(id+"F29.opExtrude","CAP_EDGE",EDGE,{"disambiguationData":[OSD([sQuery(id+"F28.wireOp",EDGE,"E50.top")])],"isStart":true});
            fillet(context, id + "F30", {"entities" : qUnion([Q0, Q1, Q2, Q3]), "radius" : 2 * mm, "tangentPropagation" : true, "allowEdgeOverflow" : false});
        }
        {
            var Q0;
            Q0=makeQuery(id+"F27.opExtrude","SWEPT_EDGE",EDGE,{"disambiguationData":[OSD([sQuery(id+"F26.wireOp",EDGE,"E36"),sQuery(id+"F26.wireOp",EDGE,"E37")])]});
            var Q1;
            Q1=makeQuery(id+"F27.opExtrude","SWEPT_EDGE",EDGE,{"disambiguationData":[OSD([sQuery(id+"F26.wireOp",EDGE,"E47.MirrorCS"),sQuery(id+"F26.wireOp",EDGE,"E48.MirrorCS")])]});
            var Q2;
            Q2=makeQuery(id+"F27.opExtrude","CAP_EDGE",EDGE,{"disambiguationData":[OSD([sQuery(id+"F26.wireOp",EDGE,"E42.MirrorCS")])],"isStart":true});
            var Q3;
            Q3=makeQuery(id+"F27.opExtrude","CAP_EDGE",EDGE,{"disambiguationData":[OSD([sQuery(id+"F26.wireOp",EDGE,"E45.MirrorCS")])],"isStart":true});
            var Q4;
            Q4=makeQuery(id+"F27.opExtrude","CAP_EDGE",EDGE,{"disambiguationData":[OSD([sQuery(id+"F26.wireOp",EDGE,"E35")])],"isStart":true});
            var Q5;
            Q5=makeQuery(id+"F27.opExtrude","CAP_EDGE",EDGE,{"disambiguationData":[OSD([sQuery(id+"F26.wireOp",EDGE,"E31")])],"isStart":true});
            var Q6;
            Q6=makeQuery(id+"F27.opExtrude","TWEAK_EDGE",EDGE,{"derivedFrom":[makeQuery(id+"F24.boolean.opBoolean","MERGE",FACE,{"derivedFrom":[makeQuery(id+"F22.boolean.opBoolean","MERGE",FACE,{"derivedFrom":[makeQuery(id+"F5.boolean.opBoolean","MERGE",FACE,{"derivedFrom":[makeQuery(id+"F3.boolean.opBoolean","MERGE",FACE,{"derivedFrom":[makeQuery(id+"F1.opExtrude","SWEPT_FACE",FACE,{"disambiguationData":[OSD([sQuery(id+"F0.wireOp",EDGE,"E0.right")])]}),makeQuery(id+"F3.opExtrude","SWEPT_FACE",FACE,{"disambiguationData":[OSD([sQuery(id+"F2.wireOp",EDGE,"E4.left")])]})]}),makeQuery(id+"F5.opExtrude","SWEPT_FACE",FACE,{"disambiguationData":[OSD([sQuery(id+"F4.wireOp",EDGE,"E5.1")])]})]}),makeQuery(id+"F22.opExtrude","SWEPT_FACE",FACE,{"disambiguationData":[OSD([sQuery(id+"F21.wireOp",EDGE,"E25.right")])]}),makeQuery(id+"F22.opExtrude","SWEPT_FACE",FACE,{"disambiguationData":[OSD([sQuery(id+"F21.wireOp",EDGE,"E26.right")])]})]}),makeQuery(id+"F24.opExtrude","SWEPT_FACE",FACE,{"disambiguationData":[OSD([sQuery(id+"F23.wireOp",EDGE,"E27.right")])]}),makeQuery(id+"F24.opExtrude","SWEPT_FACE",FACE,{"disambiguationData":[OSD([sQuery(id+"F23.wireOp",EDGE,"E28.right")])]})]}),makeQuery(id+"F26.imprint","IMPRINT",EDGE,{"derivedFrom":sQuery(id+"F26.wireOp",EDGE,"E31")})]});
            var Q7;
            Q7=makeQuery(id+"F27.opExtrude","TWEAK_EDGE",EDGE,{"derivedFrom":[makeQuery(id+"F24.boolean.opBoolean","MERGE",FACE,{"derivedFrom":[makeQuery(id+"F22.boolean.opBoolean","MERGE",FACE,{"derivedFrom":[makeQuery(id+"F5.boolean.opBoolean","MERGE",FACE,{"derivedFrom":[makeQuery(id+"F3.boolean.opBoolean","MERGE",FACE,{"derivedFrom":[makeQuery(id+"F1.opExtrude","SWEPT_FACE",FACE,{"disambiguationData":[OSD([sQuery(id+"F0.wireOp",EDGE,"E0.right")])]}),makeQuery(id+"F3.opExtrude","SWEPT_FACE",FACE,{"disambiguationData":[OSD([sQuery(id+"F2.wireOp",EDGE,"E4.left")])]})]}),makeQuery(id+"F5.opExtrude","SWEPT_FACE",FACE,{"disambiguationData":[OSD([sQuery(id+"F4.wireOp",EDGE,"E5.1")])]})]}),makeQuery(id+"F22.opExtrude","SWEPT_FACE",FACE,{"disambiguationData":[OSD([sQuery(id+"F21.wireOp",EDGE,"E25.right")])]}),makeQuery(id+"F22.opExtrude","SWEPT_FACE",FACE,{"disambiguationData":[OSD([sQuery(id+"F21.wireOp",EDGE,"E26.right")])]})]}),makeQuery(id+"F24.opExtrude","SWEPT_FACE",FACE,{"disambiguationData":[OSD([sQuery(id+"F23.wireOp",EDGE,"E27.right")])]}),makeQuery(id+"F24.opExtrude","SWEPT_FACE",FACE,{"disambiguationData":[OSD([sQuery(id+"F23.wireOp",EDGE,"E28.right")])]})]}),makeQuery(id+"F26.imprint","IMPRINT",EDGE,{"derivedFrom":sQuery(id+"F26.wireOp",EDGE,"E35")})]});
            var Q8;
            Q8=makeQuery(id+"F27.opExtrude","TWEAK_EDGE",EDGE,{"derivedFrom":[makeQuery(id+"F24.boolean.opBoolean","MERGE",FACE,{"derivedFrom":[makeQuery(id+"F22.boolean.opBoolean","MERGE",FACE,{"derivedFrom":[makeQuery(id+"F5.boolean.opBoolean","MERGE",FACE,{"derivedFrom":[makeQuery(id+"F3.boolean.opBoolean","MERGE",FACE,{"derivedFrom":[makeQuery(id+"F1.opExtrude","SWEPT_FACE",FACE,{"disambiguationData":[OSD([sQuery(id+"F0.wireOp",EDGE,"E0.right")])]}),makeQuery(id+"F3.opExtrude","SWEPT_FACE",FACE,{"disambiguationData":[OSD([sQuery(id+"F2.wireOp",EDGE,"E4.left")])]})]}),makeQuery(id+"F5.opExtrude","SWEPT_FACE",FACE,{"disambiguationData":[OSD([sQuery(id+"F4.wireOp",EDGE,"E5.1")])]})]}),makeQuery(id+"F22.opExtrude","SWEPT_FACE",FACE,{"disambiguationData":[OSD([sQuery(id+"F21.wireOp",EDGE,"E25.right")])]}),makeQuery(id+"F22.opExtrude","SWEPT_FACE",FACE,{"disambiguationData":[OSD([sQuery(id+"F21.wireOp",EDGE,"E26.right")])]})]}),makeQuery(id+"F24.opExtrude","SWEPT_FACE",FACE,{"disambiguationData":[OSD([sQuery(id+"F23.wireOp",EDGE,"E27.right")])]}),makeQuery(id+"F24.opExtrude","SWEPT_FACE",FACE,{"disambiguationData":[OSD([sQuery(id+"F23.wireOp",EDGE,"E28.right")])]})]}),makeQuery(id+"F26.imprint","IMPRINT",EDGE,{"derivedFrom":sQuery(id+"F26.wireOp",EDGE,"E42.MirrorCS")})]});
            var Q9;
            Q9=makeQuery(id+"F27.opExtrude","TWEAK_EDGE",EDGE,{"derivedFrom":[makeQuery(id+"F24.boolean.opBoolean","MERGE",FACE,{"derivedFrom":[makeQuery(id+"F22.boolean.opBoolean","MERGE",FACE,{"derivedFrom":[makeQuery(id+"F5.boolean.opBoolean","MERGE",FACE,{"derivedFrom":[makeQuery(id+"F3.boolean.opBoolean","MERGE",FACE,{"derivedFrom":[makeQuery(id+"F1.opExtrude","SWEPT_FACE",FACE,{"disambiguationData":[OSD([sQuery(id+"F0.wireOp",EDGE,"E0.right")])]}),makeQuery(id+"F3.opExtrude","SWEPT_FACE",FACE,{"disambiguationData":[OSD([sQuery(id+"F2.wireOp",EDGE,"E4.left")])]})]}),makeQuery(id+"F5.opExtrude","SWEPT_FACE",FACE,{"disambiguationData":[OSD([sQuery(id+"F4.wireOp",EDGE,"E5.1")])]})]}),makeQuery(id+"F22.opExtrude","SWEPT_FACE",FACE,{"disambiguationData":[OSD([sQuery(id+"F21.wireOp",EDGE,"E25.right")])]}),makeQuery(id+"F22.opExtrude","SWEPT_FACE",FACE,{"disambiguationData":[OSD([sQuery(id+"F21.wireOp",EDGE,"E26.right")])]})]}),makeQuery(id+"F24.opExtrude","SWEPT_FACE",FACE,{"disambiguationData":[OSD([sQuery(id+"F23.wireOp",EDGE,"E27.right")])]}),makeQuery(id+"F24.opExtrude","SWEPT_FACE",FACE,{"disambiguationData":[OSD([sQuery(id+"F23.wireOp",EDGE,"E28.right")])]})]}),makeQuery(id+"F26.imprint","IMPRINT",EDGE,{"derivedFrom":sQuery(id+"F26.wireOp",EDGE,"E45.MirrorCS")})]});
            fillet(context, id + "F31", {"entities" : qUnion([Q0, Q1, Q2, Q3, Q4, Q5, Q6, Q7, Q8, Q9]), "radius" : 1 * mm, "tangentPropagation" : true, "allowEdgeOverflow" : false});
        }
        {
            var Q0;
            Q0=qCreatedBy(makeId("Top.planeOp"),FACE);
            var sketch = newSketch(context, id + "F32", { "sketchPlane" : qUnion([Q0])});
            skLineSegment(sketch, "E51", {"start": v(-69.65, 0) * mm, "end": v(-69.65, 10) * mm});
            skLineSegment(sketch, "E52", {"start": v(-69.65, 10) * mm, "end": v(-75, 40) * mm});
            skLineSegment(sketch, "E53", {"start": v(-75, 40) * mm, "end": v(-75, 0) * mm});
            skLineSegment(sketch, "E54", {"start": v(-75, 0) * mm, "end": v(-69.65, 0) * mm});
            skLineSegment(sketch, "E55", {"start": v(0, 0) * mm, "end": v(0, 66.92) * mm, "construction": true});
            skLineSegment(sketch, "E56.MirrorCS", {"start": v(75, 40) * mm, "end": v(75, 0) * mm});
            skLineSegment(sketch, "E57.MirrorCS", {"start": v(75, 0) * mm, "end": v(69.65, 0) * mm});
            skLineSegment(sketch, "E58.MirrorCS", {"start": v(69.65, 10) * mm, "end": v(75, 40) * mm});
            skLineSegment(sketch, "E59.MirrorCS", {"start": v(69.65, 0) * mm, "end": v(69.65, 10) * mm});
            skSolve(sketch);
        }
        {
            var Q0;
            Q0 = qSketchRegion(id + "F32", true);
            extrude(context, id + "F33", {"entities" : qUnion([Q0]), "operationType" : NewBodyOperationType.REMOVE, "endBound" : BoundingType.SYMMETRIC, "oppositeDirection" : true, "depth" : 160 * mm, "offsetDistance" : 25 * mm});
        }
        {
            var Q0;
            Q0=makeQuery(id+"F27.opExtrude","SWEPT_FACE",FACE,{"disambiguationData":[OSD([sQuery(id+"F26.wireOp",EDGE,"E47.MirrorCS")])]});
            var sketch = newSketch(context, id + "F34", { "sketchPlane" : qUnion([Q0])});
            skLineSegment(sketch, "E60", {"start": v(-69.65, -5) * mm, "end": v(69.65, -5) * mm, "construction": true});
            skCircle(sketch, "E61", {"center": v(-64.65, -5) * mm, "radius": 1 * mm});
            skCircle(sketch, "E62", {"center": v(0, -5) * mm, "radius": 1 * mm});
            skCircle(sketch, "E63", {"center": v(64.65, -5) * mm, "radius": 1 * mm});
            skLineSegment(sketch, "E64", {"start": v(0, 0) * mm, "end": v(0, -15.62) * mm, "construction": true});
            skSolve(sketch);
        }
        {
            var Q0;
            Q0 = qSketchRegion(id + "F34", true);
            extrude(context, id + "F35", {"entities" : qUnion([Q0]), "operationType" : NewBodyOperationType.REMOVE, "oppositeDirection" : true, "depth" : 8 * mm, "offsetDistance" : 25 * mm});
        }
        {
            var Q0;
            Q0=makeQuery(id+"F27.opExtrude","SWEPT_FACE",FACE,{"disambiguationData":[OSD([sQuery(id+"F26.wireOp",EDGE,"E37")])]});
            var sketch = newSketch(context, id + "F36", { "sketchPlane" : qUnion([Q0])});
            skCircle(sketch, "E65.0", {"center": v(-64.65, 5) * mm, "radius": 1 * mm});
            skCircle(sketch, "E65.1", {"center": v(0, 5) * mm, "radius": 1 * mm});
            skCircle(sketch, "E65.2", {"center": v(64.65, 5) * mm, "radius": 1 * mm});
            skSolve(sketch);
        }
        {
            var Q0;
            Q0 = qSketchRegion(id + "F36", true);
            extrude(context, id + "F37", {"entities" : qUnion([Q0]), "operationType" : NewBodyOperationType.REMOVE, "oppositeDirection" : true, "depth" : 8 * mm, "offsetDistance" : 25 * mm});
        }
    });
